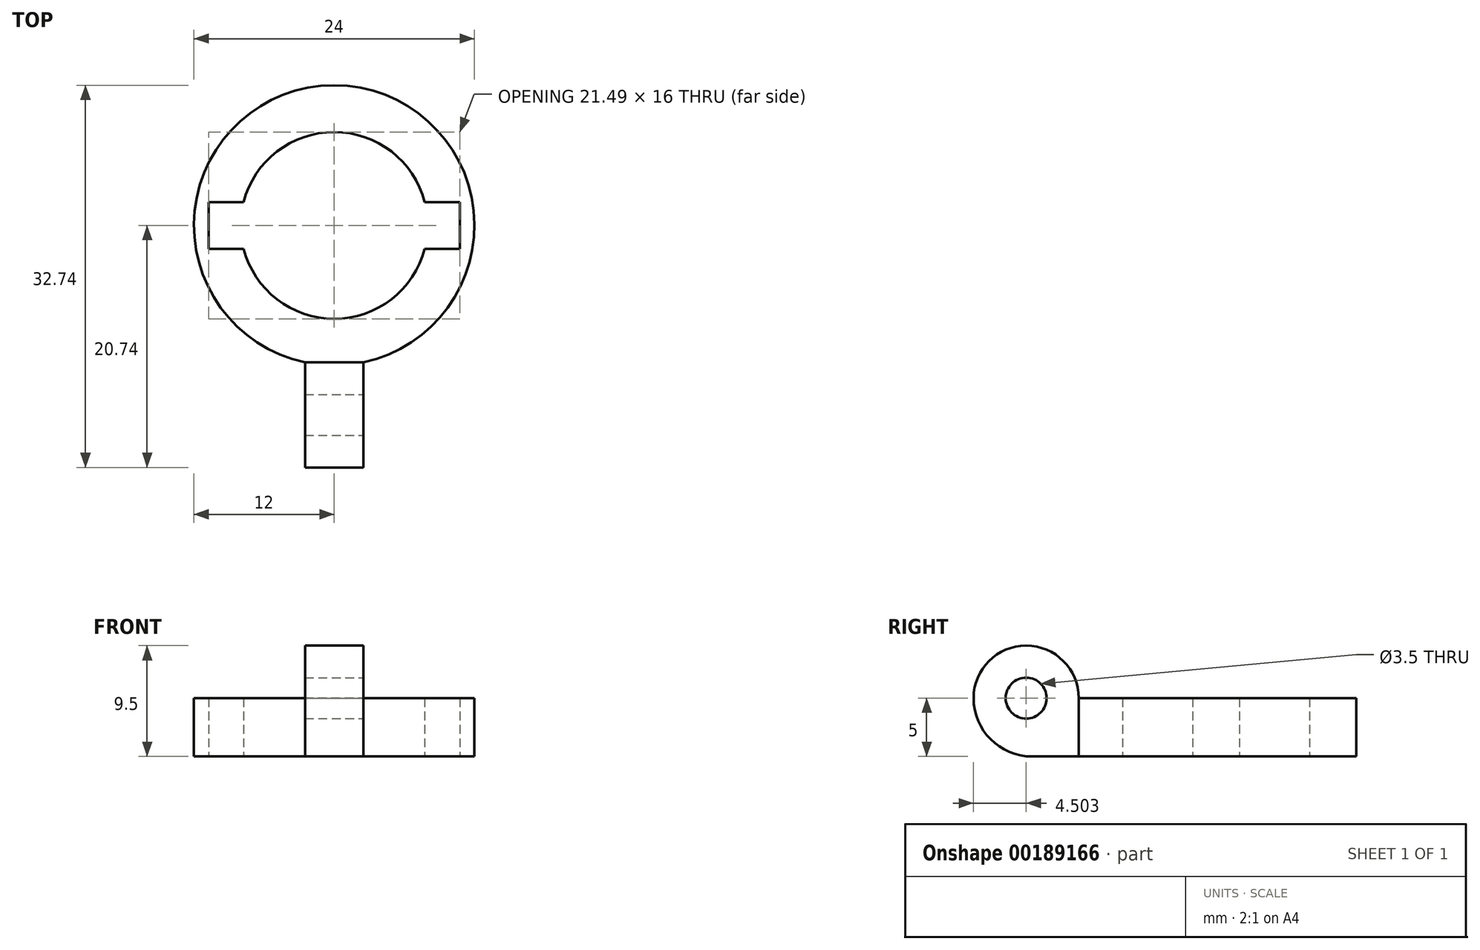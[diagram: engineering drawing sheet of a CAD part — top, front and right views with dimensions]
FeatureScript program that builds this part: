
annotation { "Feature Type Name" : "Feature", "Feature Type Description" : "" }
export const myFeature = defineFeature(function(context is Context, id is Id, definition is map)
    precondition{}
    {
        {
            var Q0;
            Q0=qCreatedBy(makeId("Top.planeOp"),FACE);
            var sketch = newSketch(context, id + "F0", { "sketchPlane" : qUnion([Q0])});
            skArc(sketch, "E0", {"start": v(-7.75, -2) * mm, "mid": v(0, -8) * mm, "end": v(7.75, -2) * mm});
            skArc(sketch, "E1", {"start": v(2.5, -11.74) * mm, "mid": v(0, 12) * mm, "end": v(-2.5, -11.74) * mm});
            skLineSegment(sketch, "E2", {"start": v(2.5, -11.74) * mm, "end": v(2.5, -20.74) * mm});
            skLineSegment(sketch, "E3", {"start": v(2.5, -20.74) * mm, "end": v(-2.5, -20.74) * mm});
            skLineSegment(sketch, "E4", {"start": v(-2.5, -20.74) * mm, "end": v(-2.5, -11.74) * mm});
            skLineSegment(sketch, "E5", {"start": v(-7.75, 2) * mm, "end": v(-10.75, 2) * mm});
            skLineSegment(sketch, "E6", {"start": v(-10.75, 2) * mm, "end": v(-10.75, -2) * mm});
            skLineSegment(sketch, "E7", {"start": v(-10.75, -2) * mm, "end": v(-7.75, -2) * mm});
            skLineSegment(sketch, "E8", {"start": v(7.75, 2) * mm, "end": v(10.75, 2) * mm});
            skLineSegment(sketch, "E9", {"start": v(10.75, 2) * mm, "end": v(10.75, -2) * mm});
            skLineSegment(sketch, "E10", {"start": v(10.75, -2) * mm, "end": v(7.75, -2) * mm});
            skArc(sketch, "E11.trimOffspring", {"start": v(7.75, 2) * mm, "mid": v(0, 8) * mm, "end": v(-7.75, 2) * mm});
            skSolve(sketch);
        }
        {
            var Q0;
            Q0=makeQuery(id+"F0.imprint","IMPRINT",FACE,{"disambiguationData":[TD([[makeQuery(id+"F0.imprint","IMPRINT",EDGE,{"derivedFrom":sQuery(id+"F0.wireOp",EDGE,"E0")}),-1.0]])]});
            extrude(context, id + "F1", {"entities" : qUnion([Q0]), "depth" : 5 * mm});
        }
        {
            var Q0;
            Q0=makeQuery(id+"F1.opExtrude","SWEPT_FACE",FACE,{"disambiguationData":[OSD([sQuery(id+"F0.wireOp",EDGE,"E2")])]});
            var sketch = newSketch(context, id + "F2", { "sketchPlane" : qUnion([Q0])});
            skCircle(sketch, "E12", {"center": v(-16.24, 5) * mm, "radius": 4.5 * mm});
            skCircle(sketch, "E13", {"center": v(-16.24, 5) * mm, "radius": 1.75 * mm});
            skSolve(sketch);
        }
        {
            var Q0;
            {var subQ1=sQuery(id+"F0.wireOp",EDGE,"E2");var subQ2=makeQuery(id+"F1.opExtrude","CAP_EDGE",EDGE,{"disambiguationData":[OSD([subQ1])],"isStart":false});var subQ5=sQuery(id+"F2.wireOp",EDGE,"E13");var subQ6=makeQuery(id+"F2.imprint","INTERSECT",VERTEX,{"disambiguationData":[OD(0.0)],"derivedFrom":[subQ2,subQ5]});Q0=makeQuery(id+"F2.imprint","IMPRINT",FACE,{"disambiguationData":[TD([[makeQuery(id+"F2.imprint","IMPRINT",EDGE,{"disambiguationData":[TD([[subQ6,-1.0]])],"derivedFrom":subQ5}),-1.0]])]});}
            extrude(context, id + "F3", {"entities" : qUnion([Q0]), "operationType" : NewBodyOperationType.ADD, "oppositeDirection" : true, "depth" : 5 * mm});
        }
        {
            var Q0;
            {var subQ0=sQuery(id+"F2.wireOp",EDGE,"E13");var subQ1=makeQuery(id+"F1.opExtrude","CAP_EDGE",EDGE,{"disambiguationData":[OSD([sQuery(id+"F0.wireOp",EDGE,"E2")])],"isStart":false});var subQ2=makeQuery(id+"F2.imprint","INTERSECT",VERTEX,{"disambiguationData":[OD(0.0)],"derivedFrom":[subQ1,subQ0]});Q0=makeQuery(id+"F2.imprint","IMPRINT",FACE,{"disambiguationData":[TD([[makeQuery(id+"F2.imprint","IMPRINT",EDGE,{"disambiguationData":[TD([[subQ2,1.0]])],"derivedFrom":subQ0}),1.0]])]});}
            extrude(context, id + "F4", {"entities" : qUnion([Q0]), "operationType" : NewBodyOperationType.REMOVE, "oppositeDirection" : true, "depth" : 25 * mm});
        }
        {
            var Q0;
            Q0=makeQuery(id+"F1.opExtrude","CAP_EDGE",EDGE,{"disambiguationData":[OSD([sQuery(id+"F0.wireOp",EDGE,"E3")])],"isStart":true});
            fillet(context, id + "F5", {"entities" : qUnion([Q0]), "radius" : 5 * mm, "tangentPropagation" : true, "allowEdgeOverflow" : false});
        }
    });
